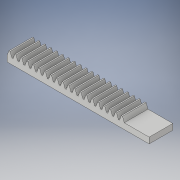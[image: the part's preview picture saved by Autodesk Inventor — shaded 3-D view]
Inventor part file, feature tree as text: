
AUTODESK INVENTOR PART (.ipt)
format: ipt  version: 2019 (Build 230136000, 136)  size: 168,448 bytes
history: native  units: mm
features: extrude x2, sketch x2, other x1, pattern_linear x1
ambient origin geometry x8: Origin, YZ Plane, XZ Plane, XY Plane, X Axis, Y Axis, Z Axis, Center Point
bodies: Body1 (feature_tree)
feature tree (6):
  other  "Твердое тело1"
  extrude  "Выдавливание1"  Depth=5.0mm
  extrude  "Выдавливание2"  Depth=120.0mm
  pattern_linear  "Прямоуг.массив1"  Count1=2 Spacing1=0.0mm
  sketch  "Эскиз1"
  sketch  "Эскиз3"
